# Revit family: BVN_BPP
name_source: partatom
category: Mechanical Equipment
units: mm (PartAtom-declared; Revit-internal decimal feet)

## family parameters
Always vertical = Yes
Cut with Voids When Loaded = No
Host = Wall
Part Type = Normal
Room Calculation Point = No
Round Connector Dimension = Use Diameter
Shared = No

## types (4) — shared parameters
Current = 0 A
Description = Plastic Fan
Frequency = 50 Hz
Insulation Class = B
Manufacturer = http://www.bahcivanmotor.com.tr
Model = EF
Pieces In Box = 5
Protection Class = 20
URL = http://www.bahcivanmotor.com.tr
Voltage = 230 V

## per-type parameters (varying)
| type | A | Air Flow | B | C | C' | D | E | ED | F | F' | Material Cover | Material Fan | Menfez | Power | Sound Pressure | Speed(d/d) | Weight | b |
| BPP 15 | 235 mm  [stored 0.770997 ft] | 360.00 m³/h | 235 mm  [stored 0.770997 ft] | 160 mm  [stored 0.524934 ft] | 53 mm | 65 mm  [stored 0.213255 ft] | 130 mm  [stored 0.426509 ft] | 65 mm  [stored 0.213255 ft] | 190 mm | 190 mm | Stainless Steel | Stainless Steel | 205 mm | 25 W | 40 | 1620 | 1.80 kg | 49 mm |
| BPP 20 | 290 mm  [stored 0.951444 ft] | 580.00 m³/h | 290 mm  [stored 0.951444 ft] | 200 mm  [stored 0.656168 ft] | 67 mm | 65 mm  [stored 0.213255 ft] | 140 mm  [stored 0.459318 ft] | 75 mm  [stored 0.246063 ft] | 240 mm  [stored 0.787402 ft] | 240 mm  [stored 0.787402 ft] | Default | <By Category> | 260 mm | 30 W | 41 | 1450 | 2.60 kg | 56 mm |
| BPP 25 | 340 mm  [stored 1.11549 ft] | 810.00 m³/h | 340 mm  [stored 1.11549 ft] | 250 mm  [stored 0.82021 ft] | 83 mm | 70 mm  [stored 0.229659 ft] | 145 mm  [stored 0.475722 ft] | 75 mm  [stored 0.246063 ft] | 290 mm  [stored 0.951444 ft] | 290 mm  [stored 0.951444 ft] | Default | <By Category> | 310 mm  [stored 1.01706 ft] | 35 W | 43 | 1375 | 2.80 kg | 56 mm |
| BPP 30 | 395 mm  [stored 1.29593 ft] | 1100.00 m³/h | 395 mm  [stored 1.29593 ft] | 300 mm | 100 mm  [stored 0.328084 ft] | 80 mm  [stored 0.262467 ft] | 155 mm  [stored 0.50853 ft] | 75 mm  [stored 0.246063 ft] | 335 mm  [stored 1.09908 ft] | 335 mm  [stored 1.09908 ft] | Default | <By Category> | 365 mm  [stored 1.19751 ft] | 40 W | 44 | 1100 | 3.20 kg | 56 mm |

note: [stored X ft] marks values corroborated as IEEE doubles in the binary element streams (Revit-internal decimal feet)

## geometry (parser evidence)
native form markers: Sweep x2
no freeform markers — native parametric forms only
